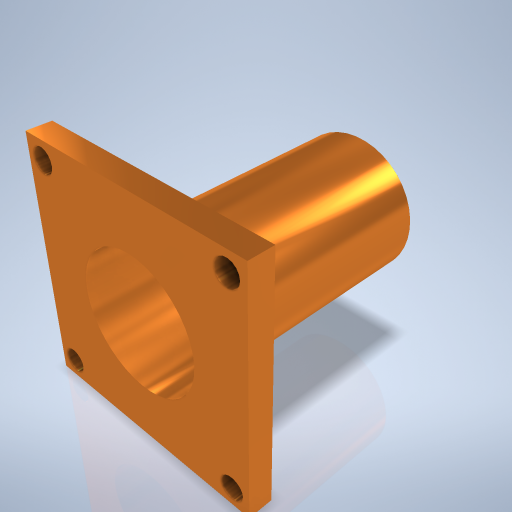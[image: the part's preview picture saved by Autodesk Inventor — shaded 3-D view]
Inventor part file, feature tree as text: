
AUTODESK INVENTOR PART (.ipt)
format: ipt  version: 2024.2 (Build 282272000, 272)  size: 291,840 bytes
history: native  units: mm
features: sketch x4, extrude x2, hole x2, chamfer x1
ambient origin geometry x8: Origin, YZ Plane, XZ Plane, XY Plane, X Axis, Y Axis, Z Axis, Center Point
bodies: Volumenkörper1 (feature_tree)
feature tree (9):
  extrude  "Extrusion1"  Depth=51.0mm TaperAngle=0.0deg
  extrude  "Extrusion2"  Depth=50.0mm
  chamfer  "Fasen1"  Distance=5.0mm
  hole  "Bohrung1"  [1 undecoded]
  hole  "Bohrung2"  [1 undecoded]
  sketch  "Skizze1"  dims[d0=28.0mm d1=51.0mm d2=0.0mm]
  sketch  "Skizze2"  dims[d3=50.0mm d4=50.0mm d5=5.0mm d6=0.0mm]
  sketch  "Skizze3"  dims[d7=1.0mm d8=2.0mm d9=45.0deg]
  sketch  "Skizze4"  dims[d10=27.0mm d11=6.0mm d12=4.0mm d13=2.0mm d14=90.0deg d15=8.0mm d16=0.0mm d17=5.0mm d18=6.0mm d19=4.0mm d20=2.0mm d21=90.0deg d22=8.0mm d23=0.0mm d30=42.248mm d31=42.248mm d32=42.248mm d33=42.248mm]
note: 2 required parameter values undecoded (feature->parameter linkage not recoverable at this tier; creation-order binding heuristic only, values carry confidence <= 0.55)
